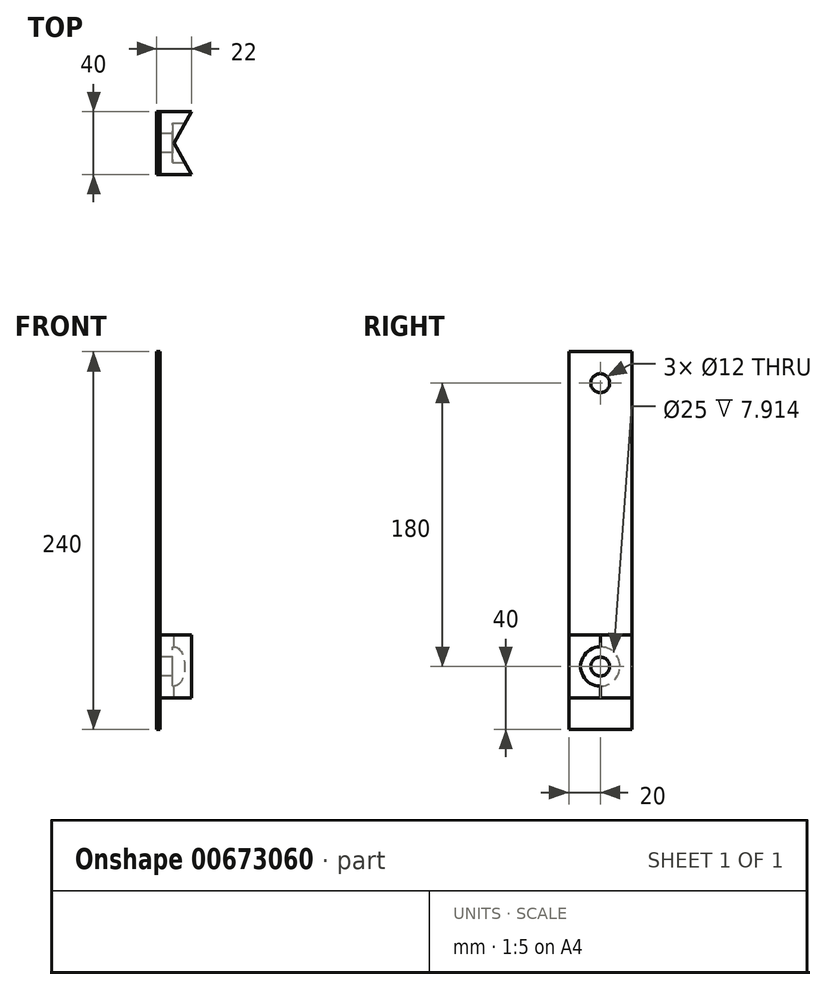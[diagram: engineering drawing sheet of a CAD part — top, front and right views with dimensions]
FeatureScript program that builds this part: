
annotation { "Feature Type Name" : "Feature", "Feature Type Description" : "" }
export const myFeature = defineFeature(function(context is Context, id is Id, definition is map)
    precondition{}
    {
        {
            var Q0;
            Q0=qCreatedBy(makeId("Right.planeOp"),FACE);
            var sketch = newSketch(context, id + "F0", { "sketchPlane" : qUnion([Q0])});
            skLineSegment(sketch, "E0.bottom", {"start": v(20, -120) * mm, "end": v(-20, -120) * mm});
            skLineSegment(sketch, "E0.top", {"start": v(20, 120) * mm, "end": v(-20, 120) * mm});
            skLineSegment(sketch, "E0.left", {"start": v(20, -120) * mm, "end": v(20, 120) * mm});
            skLineSegment(sketch, "E0.right", {"start": v(-20, -120) * mm, "end": v(-20, 120) * mm});
            skPoint(sketch, "E0.middle", {"position": v(0, 0) * mm});
            skCircle(sketch, "E1", {"center": v(0, 100) * mm, "radius": 6 * mm});
            skCircle(sketch, "E2", {"center": v(0, -80) * mm, "radius": 6 * mm});
            skLineSegment(sketch, "E3.bottom", {"start": v(20, -100) * mm, "end": v(-20, -100) * mm});
            skLineSegment(sketch, "E3.top", {"start": v(20, -60) * mm, "end": v(-20, -60) * mm});
            skLineSegment(sketch, "E3.left", {"start": v(20, -100) * mm, "end": v(20, -60) * mm});
            skLineSegment(sketch, "E3.right", {"start": v(-20, -100) * mm, "end": v(-20, -60) * mm});
            skCircle(sketch, "E4", {"center": v(0, -80) * mm, "radius": 12.5 * mm, "construction": true});
            skSolve(sketch);
        }
        {
            var Q0;
            Q0=makeQuery(id+"F0.imprint","IMPRINT",FACE,{"disambiguationData":[TD([[makeQuery(id+"F0.imprint","IMPRINT",EDGE,{"derivedFrom":sQuery(id+"F0.wireOp",EDGE,"E0.bottom")}),-1.0]])]});
            var Q1;
            {var subQ1=sQuery(id+"F0.wireOp",EDGE,"E0.top");Q1=makeQuery(id+"F0.imprint","IMPRINT",FACE,{"disambiguationData":[TD([[makeQuery(id+"F0.imprint","IMPRINT",EDGE,{"derivedFrom":subQ1}),1.0]])]});}
            var Q2;
            Q2=makeQuery(id+"F0.imprint","IMPRINT",FACE,{"disambiguationData":[TD([[makeQuery(id+"F0.imprint","IMPRINT",EDGE,{"derivedFrom":sQuery(id+"F0.wireOp",EDGE,"E2")}),-1.0]])]});
            extrude(context, id + "F1", {"entities" : qUnion([Q0, Q1, Q2]), "oppositeDirection" : true, "depth" : 2 * mm, "offsetDistance" : 25 * mm});
        }
        {
            var Q0;
            Q0=makeQuery(id+"F0.imprint","IMPRINT",FACE,{"disambiguationData":[TD([[makeQuery(id+"F0.imprint","IMPRINT",EDGE,{"derivedFrom":sQuery(id+"F0.wireOp",EDGE,"E2")}),-1.0]])]});
            extrude(context, id + "F2", {"entities" : qUnion([Q0]), "depth" : 20 * mm, "offsetDistance" : 25 * mm});
        }
        {
            var Q0;
            Q0=makeQuery(id+"F2.opExtrude","CAP_FACE",FACE,{"disambiguationData":[OSD([sQuery(id+"F0.wireOp",EDGE,"E2"),sQuery(id+"F0.wireOp",EDGE,"E3.bottom"),sQuery(id+"F0.wireOp",EDGE,"E3.top"),sQuery(id+"F0.wireOp",EDGE,"E3.left"),sQuery(id+"F0.wireOp",EDGE,"E3.right")])],"isStart":false});
            var sketch = newSketch(context, id + "F3", { "sketchPlane" : qUnion([Q0])});
            skCircle(sketch, "E5", {"center": v(0, -80) * mm, "radius": 12.5 * mm});
            skSolve(sketch);
        }
        {
            var Q0;
            Q0=makeQuery(id+"F3.imprint","IMPRINT",FACE,{"disambiguationData":[TD([[makeQuery(id+"F3.imprint","IMPRINT",EDGE,{"derivedFrom":sQuery(id+"F3.wireOp",EDGE,"E5")}),1.0]])]});
            extrude(context, id + "F4", {"entities" : qUnion([Q0]), "operationType" : NewBodyOperationType.REMOVE, "oppositeDirection" : true, "depth" : 12 * mm, "offsetDistance" : 25 * mm});
        }
        {
            var Q0;
            Q0=makeQuery(id+"F2.opExtrude","SWEPT_FACE",FACE,{"disambiguationData":[OSD([sQuery(id+"F0.wireOp",EDGE,"E3.top")])]});
            var sketch = newSketch(context, id + "F5", { "sketchPlane" : qUnion([Q0])});
            skCircle(sketch, "E6", {"center": v(35, 0) * mm, "radius": 22.5 * mm, "construction": true});
            skLineSegment(sketch, "E7", {"start": v(20, -20) * mm, "end": v(9.04, 0) * mm});
            skLineSegment(sketch, "E8", {"start": v(9.04, 0) * mm, "end": v(20, 20) * mm});
            skSolve(sketch);
        }
        {
            var Q0;
            Q0=makeQuery(id+"F5.imprint","IMPRINT",FACE,{"disambiguationData":[TD([[makeQuery(id+"F5.imprint","IMPRINT",EDGE,{"derivedFrom":sQuery(id+"F5.wireOp",EDGE,"E7")}),-1.0]])]});
            extrude(context, id + "F6", {"entities" : qUnion([Q0]), "operationType" : NewBodyOperationType.REMOVE, "endBound" : BoundingType.THROUGH_ALL, "oppositeDirection" : true, "depth" : 25 * mm, "offsetDistance" : 25 * mm});
        }
    });
